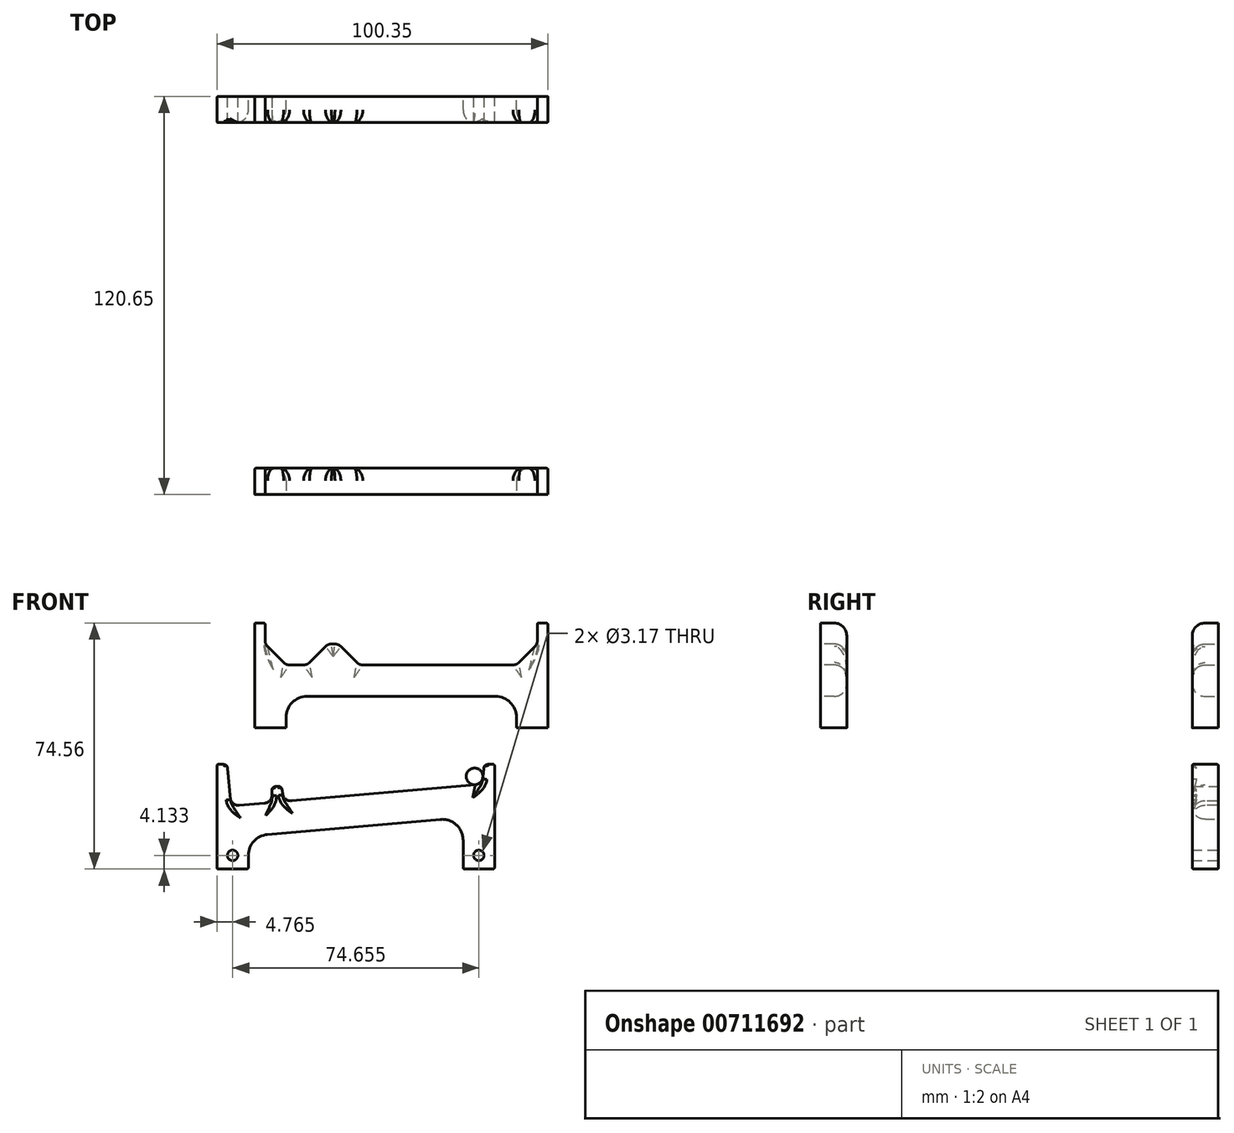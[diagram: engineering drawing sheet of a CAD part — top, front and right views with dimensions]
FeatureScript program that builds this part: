
annotation { "Feature Type Name" : "Feature", "Feature Type Description" : "" }
export const myFeature = defineFeature(function(context is Context, id is Id, definition is map)
    precondition{}
    {
        {
            var Q0;
            Q0=qCreatedBy(makeId("Front.planeOp"),FACE);
            var sketch = newSketch(context, id + "F0", { "sketchPlane" : qUnion([Q0])});
            skLineSegment(sketch, "E0", {"start": v(-44.45, 0) * mm, "end": v(-44.45, 25.4) * mm});
            skLineSegment(sketch, "E1", {"start": v(-28.58, 19.05) * mm, "end": v(-22.23, 25.4) * mm});
            skLineSegment(sketch, "E2", {"start": v(-22.23, 25.4) * mm, "end": v(-19.05, 25.4) * mm});
            skLineSegment(sketch, "E3", {"start": v(-19.05, 25.4) * mm, "end": v(-12.7, 19.05) * mm});
            skLineSegment(sketch, "E4", {"start": v(-12.7, 19.05) * mm, "end": v(34.92, 19.05) * mm});
            skLineSegment(sketch, "E5", {"start": v(34.92, 19.05) * mm, "end": v(41.28, 25.4) * mm});
            skLineSegment(sketch, "E6", {"start": v(44.45, 25.4) * mm, "end": v(44.45, 0) * mm});
            skLineSegment(sketch, "E7", {"start": v(-41.28, 25.4) * mm, "end": v(-34.93, 19.05) * mm});
            skLineSegment(sketch, "E8", {"start": v(-34.93, 19.05) * mm, "end": v(-28.58, 19.05) * mm});
            skLineSegment(sketch, "E9", {"start": v(-44.45, 25.4) * mm, "end": v(-44.45, 31.75) * mm});
            skLineSegment(sketch, "E10", {"start": v(-44.45, 31.75) * mm, "end": v(-41.28, 31.75) * mm});
            skLineSegment(sketch, "E11", {"start": v(-41.28, 31.75) * mm, "end": v(-41.28, 25.4) * mm});
            skLineSegment(sketch, "E12", {"start": v(44.45, 25.4) * mm, "end": v(44.45, 31.75) * mm});
            skLineSegment(sketch, "E13", {"start": v(44.45, 31.75) * mm, "end": v(41.28, 31.75) * mm});
            skLineSegment(sketch, "E14", {"start": v(41.28, 31.75) * mm, "end": v(41.28, 25.4) * mm});
            skLineSegment(sketch, "E15", {"start": v(-44.45, 0) * mm, "end": v(-34.93, 0) * mm});
            skLineSegment(sketch, "E16", {"start": v(44.45, 0) * mm, "end": v(34.92, 0) * mm});
            skLineSegment(sketch, "E17", {"start": v(-34.93, 0) * mm, "end": v(-34.93, 3.17) * mm});
            skLineSegment(sketch, "E18", {"start": v(34.92, 3.18) * mm, "end": v(34.92, 0) * mm});
            skPoint(sketch, "E19.visualSharp", {"position": v(-34.93, 9.52) * mm});
            skArc(sketch, "E19.filletArc", {"start": v(-28.58, 9.52) * mm, "mid": v(-33.07, 7.67) * mm, "end": v(-34.93, 3.17) * mm});
            skPoint(sketch, "E20.visualSharp", {"position": v(34.93, 9.53) * mm});
            skArc(sketch, "E20.filletArc", {"start": v(34.92, 3.18) * mm, "mid": v(33.07, 7.67) * mm, "end": v(28.58, 9.53) * mm});
            skLineSegment(sketch, "E21", {"start": v(-28.58, 9.52) * mm, "end": v(0, 9.52) * mm});
            skLineSegment(sketch, "E22", {"start": v(0, 9.52) * mm, "end": v(28.58, 9.53) * mm});
            skSolve(sketch);
        }
        {
            var Q0;
            Q0=makeQuery(id+"F0.imprint","IMPRINT",FACE,{"disambiguationData":[TD([[makeQuery(id+"F0.imprint","IMPRINT",EDGE,{"derivedFrom":sQuery(id+"F0.wireOp",EDGE,"E0")}),-1.0]])]});
            extrude(context, id + "F1", {"entities" : qUnion([Q0]), "depth" : 7.94 * mm, "offsetDistance" : 25.4 * mm});
        }
        {
            var Q0;
            Q0=makeQuery(id+"F1.opExtrude","CAP_EDGE",EDGE,{"disambiguationData":[OSD([sQuery(id+"F0.wireOp",EDGE,"E7")])],"isStart":false});
            var Q1;
            Q1=makeQuery(id+"F1.opExtrude","CAP_EDGE",EDGE,{"disambiguationData":[OSD([sQuery(id+"F0.wireOp",EDGE,"E8")])],"isStart":false});
            var Q2;
            Q2=makeQuery(id+"F1.opExtrude","CAP_EDGE",EDGE,{"disambiguationData":[OSD([sQuery(id+"F0.wireOp",EDGE,"E1")])],"isStart":false});
            var Q3;
            Q3=makeQuery(id+"F1.opExtrude","CAP_EDGE",EDGE,{"disambiguationData":[OSD([sQuery(id+"F0.wireOp",EDGE,"E2")])],"isStart":false});
            var Q4;
            Q4=makeQuery(id+"F1.opExtrude","CAP_EDGE",EDGE,{"disambiguationData":[OSD([sQuery(id+"F0.wireOp",EDGE,"E3")])],"isStart":false});
            var Q5;
            Q5=makeQuery(id+"F1.opExtrude","CAP_EDGE",EDGE,{"disambiguationData":[OSD([sQuery(id+"F0.wireOp",EDGE,"E4")])],"isStart":false});
            var Q6;
            Q6=makeQuery(id+"F1.opExtrude","CAP_EDGE",EDGE,{"disambiguationData":[OSD([sQuery(id+"F0.wireOp",EDGE,"E5")])],"isStart":false});
            var Q7;
            Q7=makeQuery(id+"F1.opExtrude","CAP_EDGE",EDGE,{"disambiguationData":[OSD([sQuery(id+"F0.wireOp",EDGE,"E10")])],"isStart":false});
            var Q8;
            Q8=makeQuery(id+"F1.opExtrude","CAP_EDGE",EDGE,{"disambiguationData":[OSD([sQuery(id+"F0.wireOp",EDGE,"E13")])],"isStart":false});
            var Q9;
            Q9=makeQuery(id+"F1.opExtrude","CAP_EDGE",EDGE,{"disambiguationData":[OSD([sQuery(id+"F0.wireOp",EDGE,"E21"),sQuery(id+"F0.wireOp",EDGE,"E22")])],"isStart":false});
            fillet(context, id + "F2", {"entities" : qUnion([Q0, Q1, Q2, Q3, Q4, Q5, Q6, Q7, Q8, Q9]), "radius" : 3.8 * mm, "tangentPropagation" : true, "allowEdgeOverflow" : false});
        }
        {
            var Q0;
            Q0=makeQuery(id+"F1.opExtrude","SWEPT_EDGE",EDGE,{"disambiguationData":[OSD([sQuery(id+"F0.wireOp",EDGE,"E1"),sQuery(id+"F0.wireOp",EDGE,"E2")])]});
            var Q1;
            Q1=makeQuery(id+"F1.opExtrude","SWEPT_EDGE",EDGE,{"disambiguationData":[OSD([sQuery(id+"F0.wireOp",EDGE,"E2"),sQuery(id+"F0.wireOp",EDGE,"E3")])]});
            var Q2;
            Q2=makeQuery(id+"F1.opExtrude","SWEPT_EDGE",EDGE,{"disambiguationData":[OSD([sQuery(id+"F0.wireOp",EDGE,"E1"),sQuery(id+"F0.wireOp",EDGE,"E8")])]});
            var Q3;
            Q3=makeQuery(id+"F1.opExtrude","SWEPT_EDGE",EDGE,{"disambiguationData":[OSD([sQuery(id+"F0.wireOp",EDGE,"E7"),sQuery(id+"F0.wireOp",EDGE,"E8")])]});
            var Q4;
            Q4=makeQuery(id+"F1.opExtrude","SWEPT_EDGE",EDGE,{"disambiguationData":[OSD([sQuery(id+"F0.wireOp",EDGE,"E3"),sQuery(id+"F0.wireOp",EDGE,"E4")])]});
            var Q5;
            Q5=makeQuery(id+"F1.opExtrude","SWEPT_EDGE",EDGE,{"disambiguationData":[OSD([sQuery(id+"F0.wireOp",EDGE,"E4"),sQuery(id+"F0.wireOp",EDGE,"E5")])]});
            var Q6;
            Q6=makeQuery(id+"F1.opExtrude","SWEPT_EDGE",EDGE,{"disambiguationData":[OSD([sQuery(id+"F0.wireOp",EDGE,"E5"),sQuery(id+"F0.wireOp",EDGE,"E14")])]});
            var Q7;
            Q7=makeQuery(id+"F1.opExtrude","SWEPT_EDGE",EDGE,{"disambiguationData":[OSD([sQuery(id+"F0.wireOp",EDGE,"E7"),sQuery(id+"F0.wireOp",EDGE,"E11")])]});
            fillet(context, id + "F3", {"entities" : qUnion([Q0, Q1, Q2, Q3, Q4, Q5, Q6, Q7]), "radius" : 2.54 * mm, "tangentPropagation" : true, "allowEdgeOverflow" : false});
        }
        {
            var Q0;
            Q0=makeQuery(id+"F1.opExtrude","CAP_EDGE",EDGE,{"disambiguationData":[OSD([sQuery(id+"F0.wireOp",EDGE,"E0"),sQuery(id+"F0.wireOp",EDGE,"E9")])],"isStart":false});
            var Q1;
            Q1=makeQuery(id+"F1.opExtrude","CAP_EDGE",EDGE,{"disambiguationData":[OSD([sQuery(id+"F0.wireOp",EDGE,"E6"),sQuery(id+"F0.wireOp",EDGE,"E12")])],"isStart":false});
            var Q2;
            Q2=makeQuery(id+"F2.opFillet","BLEND_EDGE",EDGE,{"blendedFrom":[makeQuery(id+"F1.opExtrude","CAP_EDGE",EDGE,{"disambiguationData":[OSD([sQuery(id+"F0.wireOp",EDGE,"E13")])],"isStart":false}),makeQuery(id+"F1.opExtrude","SWEPT_FACE",FACE,{"disambiguationData":[OSD([sQuery(id+"F0.wireOp",EDGE,"E14")])]})],"blendedInto":[makeQuery(id+"F1.opExtrude","SWEPT_FACE",FACE,{"disambiguationData":[OSD([sQuery(id+"F0.wireOp",EDGE,"E14")])]})]});
            var Q3;
            Q3=makeQuery(id+"F2.opFillet","BLEND_EDGE",EDGE,{"blendedFrom":[makeQuery(id+"F1.opExtrude","CAP_EDGE",EDGE,{"disambiguationData":[OSD([sQuery(id+"F0.wireOp",EDGE,"E10")])],"isStart":false}),makeQuery(id+"F1.opExtrude","SWEPT_FACE",FACE,{"disambiguationData":[OSD([sQuery(id+"F0.wireOp",EDGE,"E11")])]})],"blendedInto":[makeQuery(id+"F1.opExtrude","SWEPT_FACE",FACE,{"disambiguationData":[OSD([sQuery(id+"F0.wireOp",EDGE,"E11")])]})]});
            fillet(context, id + "F4", {"entities" : qUnion([Q0, Q1, Q2, Q3]), "radius" : 0.38 * mm, "tangentPropagation" : true, "allowEdgeOverflow" : false});
        }
        {
            var Q0;
            Q0=makeQuery(id+"F1.opExtrude","SWEPT_BODY",BODY,{"disambiguationData":[OSD([sQuery(id+"F0.wireOp",EDGE,"E0"),sQuery(id+"F0.wireOp",EDGE,"E1"),sQuery(id+"F0.wireOp",EDGE,"E2"),sQuery(id+"F0.wireOp",EDGE,"E3"),sQuery(id+"F0.wireOp",EDGE,"E4"),sQuery(id+"F0.wireOp",EDGE,"E5"),sQuery(id+"F0.wireOp",EDGE,"E6"),sQuery(id+"F0.wireOp",EDGE,"E7"),sQuery(id+"F0.wireOp",EDGE,"E8"),sQuery(id+"F0.wireOp",EDGE,"E9"),sQuery(id+"F0.wireOp",EDGE,"E10"),sQuery(id+"F0.wireOp",EDGE,"E11"),sQuery(id+"F0.wireOp",EDGE,"E12"),sQuery(id+"F0.wireOp",EDGE,"E13"),sQuery(id+"F0.wireOp",EDGE,"E14"),sQuery(id+"F0.wireOp",EDGE,"E15"),sQuery(id+"F0.wireOp",EDGE,"E16"),sQuery(id+"F0.wireOp",EDGE,"E17"),sQuery(id+"F0.wireOp",EDGE,"E18"),sQuery(id+"F0.wireOp",EDGE,"E19.filletArc"),sQuery(id+"F0.wireOp",EDGE,"E20.filletArc"),sQuery(id+"F0.wireOp",EDGE,"E21"),sQuery(id+"F0.wireOp",EDGE,"E22")])]});
            var Q1;
            Q1=qCreatedBy(makeId("Front.planeOp"),FACE);
            mirror(context, id + "F5", {"entities" : qUnion([Q0]), "mirrorPlane" : qUnion([Q1])});
        }
        {
            var Q0;
            Q0=makeQuery(id+"F5.opPattern","COPY",BODY,{"derivedFrom":makeQuery(id+"F1.opExtrude","SWEPT_BODY",BODY,{"disambiguationData":[OSD([sQuery(id+"F0.wireOp",EDGE,"E0"),sQuery(id+"F0.wireOp",EDGE,"E1"),sQuery(id+"F0.wireOp",EDGE,"E2"),sQuery(id+"F0.wireOp",EDGE,"E3"),sQuery(id+"F0.wireOp",EDGE,"E4"),sQuery(id+"F0.wireOp",EDGE,"E5"),sQuery(id+"F0.wireOp",EDGE,"E6"),sQuery(id+"F0.wireOp",EDGE,"E7"),sQuery(id+"F0.wireOp",EDGE,"E8"),sQuery(id+"F0.wireOp",EDGE,"E9"),sQuery(id+"F0.wireOp",EDGE,"E10"),sQuery(id+"F0.wireOp",EDGE,"E11"),sQuery(id+"F0.wireOp",EDGE,"E12"),sQuery(id+"F0.wireOp",EDGE,"E13"),sQuery(id+"F0.wireOp",EDGE,"E14"),sQuery(id+"F0.wireOp",EDGE,"E15"),sQuery(id+"F0.wireOp",EDGE,"E16"),sQuery(id+"F0.wireOp",EDGE,"E17"),sQuery(id+"F0.wireOp",EDGE,"E18"),sQuery(id+"F0.wireOp",EDGE,"E19.filletArc"),sQuery(id+"F0.wireOp",EDGE,"E20.filletArc"),sQuery(id+"F0.wireOp",EDGE,"E21"),sQuery(id+"F0.wireOp",EDGE,"E22")])]}),"instanceName":"1"});
            var Q1;
            Q1=qCreatedBy(makeId("Front.planeOp"),FACE);
            transform(context, id + "F6", {"entities" : qUnion([Q0]), "transformType" : TransformType.TRANSLATION_DISTANCE, "transformDirection" : qUnion([Q1]), "distance" : 120.65 * mm, "makeCopy" : false});
        }
        {
            var Q0;
            Q0=qCreatedBy(makeId("Front.planeOp"),FACE);
            var sketch = newSketch(context, id + "F7", { "sketchPlane" : qUnion([Q0])});
            skLineSegment(sketch, "E23", {"start": v(-39.38, -17.9) * mm, "end": v(-36.22, -17.63) * mm});
            skLineSegment(sketch, "E24", {"start": v(-39.38, -17.9) * mm, "end": v(-38.96, -22.65) * mm});
            skLineSegment(sketch, "E25", {"start": v(-38.96, -22.65) * mm, "end": v(-51.62, -23.76) * mm});
            skLineSegment(sketch, "E26", {"start": v(-51.62, -23.76) * mm, "end": v(-52.72, -11.1) * mm});
            skLineSegment(sketch, "E27", {"start": v(-52.72, -11.1) * mm, "end": v(-55.9, -11.1) * mm});
            skLineSegment(sketch, "E28", {"start": v(-55.9, -11.1) * mm, "end": v(-55.9, -42.8) * mm});
            skLineSegment(sketch, "E29", {"start": v(-36.22, -17.63) * mm, "end": v(-35.8, -22.37) * mm});
            skLineSegment(sketch, "E30", {"start": v(-55.9, -42.8) * mm, "end": v(-46.37, -42.8) * mm});
            skLineSegment(sketch, "E31", {"start": v(-46.37, -42.8) * mm, "end": v(-46.37, -38.68) * mm});
            skLineSegment(sketch, "E32", {"start": v(28.28, -42.8) * mm, "end": v(18.76, -42.8) * mm});
            skLineSegment(sketch, "E33", {"start": v(18.76, -42.8) * mm, "end": v(18.76, -38.68) * mm});
            skLineSegment(sketch, "E34", {"start": v(18.76, -38.68) * mm, "end": v(18.76, -34.09) * mm});
            skLineSegment(sketch, "E35", {"start": v(11.85, -27.76) * mm, "end": v(-40.58, -32.35) * mm});
            skLineSegment(sketch, "E36", {"start": v(28.28, -42.8) * mm, "end": v(28.28, -11.1) * mm});
            skLineSegment(sketch, "E37", {"start": v(28.28, -11.1) * mm, "end": v(25.1, -11.1) * mm});
            skLineSegment(sketch, "E38", {"start": v(-35.8, -22.37) * mm, "end": v(24.58, -17.09) * mm});
            skLineSegment(sketch, "E39", {"start": v(25.1, -11.1) * mm, "end": v(24.58, -17.09) * mm});
            skPoint(sketch, "E40.visualSharp", {"position": v(-46.37, -32.86) * mm});
            skArc(sketch, "E40.filletArc", {"start": v(-40.58, -32.35) * mm, "mid": v(-44.7, -34.39) * mm, "end": v(-46.37, -38.68) * mm});
            skPoint(sketch, "E41.visualSharp", {"position": v(18.76, -27.16) * mm});
            skArc(sketch, "E41.filletArc", {"start": v(18.76, -34.09) * mm, "mid": v(16.7, -29.4) * mm, "end": v(11.85, -27.76) * mm});
            skCircle(sketch, "E42", {"center": v(-51.14, -38.68) * mm, "radius": 1.59 * mm});
            skPoint(sketch, "E43", {"position": v(-51.14, -42.8) * mm});
            skCircle(sketch, "E44", {"center": v(23.52, -38.68) * mm, "radius": 1.59 * mm});
            skPoint(sketch, "E45", {"position": v(23.52, -42.8) * mm});
            skSolve(sketch);
        }
        {
            var Q0;
            Q0=makeQuery(id+"F7.imprint","IMPRINT",FACE,{"disambiguationData":[TD([[makeQuery(id+"F7.imprint","IMPRINT",EDGE,{"derivedFrom":sQuery(id+"F7.wireOp",EDGE,"E23")}),-1.0]])]});
            extrude(context, id + "F8", {"entities" : qUnion([Q0]), "depth" : 7.94 * mm, "offsetDistance" : 25.4 * mm});
        }
        {
            var Q0;
            Q0=makeQuery(id+"F8.opExtrude","CAP_EDGE",EDGE,{"disambiguationData":[OSD([sQuery(id+"F7.wireOp",EDGE,"E25")])],"isStart":false});
            var Q1;
            Q1=makeQuery(id+"F8.opExtrude","CAP_EDGE",EDGE,{"disambiguationData":[OSD([sQuery(id+"F7.wireOp",EDGE,"E38")])],"isStart":false});
            var Q2;
            Q2=makeQuery(id+"F8.opExtrude","CAP_EDGE",EDGE,{"disambiguationData":[OSD([sQuery(id+"F7.wireOp",EDGE,"E35")])],"isStart":false});
            fillet(context, id + "F9", {"entities" : qUnion([Q0, Q1, Q2]), "radius" : 3.8 * mm, "tangentPropagation" : true, "allowEdgeOverflow" : false});
        }
        {
            var Q0;
            Q0=makeQuery(id+"F8.opExtrude","SWEPT_EDGE",EDGE,{"disambiguationData":[OSD([sQuery(id+"F7.wireOp",EDGE,"E25"),sQuery(id+"F7.wireOp",EDGE,"E26")])]});
            var Q1;
            Q1=makeQuery(id+"F8.opExtrude","SWEPT_EDGE",EDGE,{"disambiguationData":[OSD([sQuery(id+"F7.wireOp",EDGE,"E24"),sQuery(id+"F7.wireOp",EDGE,"E25")])]});
            var Q2;
            Q2=makeQuery(id+"F8.opExtrude","SWEPT_EDGE",EDGE,{"disambiguationData":[OSD([sQuery(id+"F7.wireOp",EDGE,"E29"),sQuery(id+"F7.wireOp",EDGE,"E38")])]});
            var Q3;
            Q3=makeQuery(id+"F8.opExtrude","SWEPT_EDGE",EDGE,{"disambiguationData":[OSD([sQuery(id+"F7.wireOp",EDGE,"E38"),sQuery(id+"F7.wireOp",EDGE,"E39")])]});
            fillet(context, id + "F10", {"entities" : qUnion([Q0, Q1, Q2, Q3]), "radius" : 2.54 * mm, "tangentPropagation" : true, "allowEdgeOverflow" : false});
        }
        {
            var Q0;
            Q0=makeQuery(id+"F8.opExtrude","CAP_EDGE",EDGE,{"disambiguationData":[OSD([sQuery(id+"F7.wireOp",EDGE,"E26")])],"isStart":false});
            var Q1;
            Q1=makeQuery(id+"F8.opExtrude","SWEPT_EDGE",EDGE,{"disambiguationData":[OSD([sQuery(id+"F7.wireOp",EDGE,"E26"),sQuery(id+"F7.wireOp",EDGE,"E27")])]});
            var Q2;
            Q2=makeQuery(id+"F8.opExtrude","SWEPT_EDGE",EDGE,{"disambiguationData":[OSD([sQuery(id+"F7.wireOp",EDGE,"E23"),sQuery(id+"F7.wireOp",EDGE,"E24")])]});
            var Q3;
            Q3=makeQuery(id+"F8.opExtrude","SWEPT_EDGE",EDGE,{"disambiguationData":[OSD([sQuery(id+"F7.wireOp",EDGE,"E23"),sQuery(id+"F7.wireOp",EDGE,"E29")])]});
            var Q4;
            Q4=makeQuery(id+"F8.opExtrude","SWEPT_EDGE",EDGE,{"disambiguationData":[OSD([sQuery(id+"F7.wireOp",EDGE,"E37"),sQuery(id+"F7.wireOp",EDGE,"E39")])]});
            var Q5;
            Q5=makeQuery(id+"F8.opExtrude","CAP_EDGE",EDGE,{"disambiguationData":[OSD([sQuery(id+"F7.wireOp",EDGE,"E39")])],"isStart":false});
            var Q6;
            Q6=makeQuery(id+"F8.opExtrude","CAP_EDGE",EDGE,{"disambiguationData":[OSD([sQuery(id+"F7.wireOp",EDGE,"E24")])],"isStart":false});
            var Q7;
            Q7=makeQuery(id+"F8.opExtrude","CAP_EDGE",EDGE,{"disambiguationData":[OSD([sQuery(id+"F7.wireOp",EDGE,"E29")])],"isStart":false});
            fillet(context, id + "F11", {"entities" : qUnion([Q0, Q1, Q2, Q3, Q4, Q5, Q6, Q7]), "radius" : 1.27 * mm, "tangentPropagation" : true, "allowEdgeOverflow" : false});
        }
        {
            var Q0;
            Q0=makeQuery(id+"F8.opExtrude","CAP_EDGE",EDGE,{"disambiguationData":[OSD([sQuery(id+"F7.wireOp",EDGE,"E27")])],"isStart":false});
            var Q1;
            Q1=makeQuery(id+"F8.opExtrude","SWEPT_EDGE",EDGE,{"disambiguationData":[OSD([sQuery(id+"F7.wireOp",EDGE,"E27"),sQuery(id+"F7.wireOp",EDGE,"E28")])]});
            var Q2;
            Q2=makeQuery(id+"F8.opExtrude","CAP_EDGE",EDGE,{"disambiguationData":[OSD([sQuery(id+"F7.wireOp",EDGE,"E28")])],"isStart":false});
            var Q3;
            Q3=makeQuery(id+"F8.opExtrude","CAP_EDGE",EDGE,{"disambiguationData":[OSD([sQuery(id+"F7.wireOp",EDGE,"E36")])],"isStart":false});
            var Q4;
            Q4=makeQuery(id+"F8.opExtrude","SWEPT_EDGE",EDGE,{"disambiguationData":[OSD([sQuery(id+"F7.wireOp",EDGE,"E36"),sQuery(id+"F7.wireOp",EDGE,"E37")])]});
            var Q5;
            Q5=makeQuery(id+"F8.opExtrude","CAP_EDGE",EDGE,{"disambiguationData":[OSD([sQuery(id+"F7.wireOp",EDGE,"E23")])],"isStart":false});
            var Q6;
            Q6=makeQuery(id+"F8.opExtrude","CAP_EDGE",EDGE,{"disambiguationData":[OSD([sQuery(id+"F7.wireOp",EDGE,"E37")])],"isStart":false});
            var Q7;
            Q7=makeQuery(id+"F8.opExtrude","CAP_EDGE",EDGE,{"disambiguationData":[OSD([sQuery(id+"F7.wireOp",EDGE,"E36")])],"isStart":true});
            var Q8;
            Q8=makeQuery(id+"F8.opExtrude","SWEPT_EDGE",EDGE,{"disambiguationData":[OSD([sQuery(id+"F7.wireOp",EDGE,"E32"),sQuery(id+"F7.wireOp",EDGE,"E36")])]});
            var Q9;
            Q9=makeQuery(id+"F8.opExtrude","CAP_EDGE",EDGE,{"disambiguationData":[OSD([sQuery(id+"F7.wireOp",EDGE,"E32")])],"isStart":true});
            var Q10;
            Q10=makeQuery(id+"F8.opExtrude","CAP_EDGE",EDGE,{"disambiguationData":[OSD([sQuery(id+"F7.wireOp",EDGE,"E35")])],"isStart":true});
            var Q11;
            Q11=makeQuery(id+"F8.opExtrude","CAP_EDGE",EDGE,{"disambiguationData":[OSD([sQuery(id+"F7.wireOp",EDGE,"E38")])],"isStart":true});
            var Q12;
            Q12=makeQuery(id+"F8.opExtrude","CAP_EDGE",EDGE,{"disambiguationData":[OSD([sQuery(id+"F7.wireOp",EDGE,"E28")])],"isStart":true});
            var Q13;
            Q13=makeQuery(id+"F8.opExtrude","CAP_EDGE",EDGE,{"disambiguationData":[OSD([sQuery(id+"F7.wireOp",EDGE,"E30")])],"isStart":true});
            var Q14;
            Q14=makeQuery(id+"F8.opExtrude","SWEPT_EDGE",EDGE,{"disambiguationData":[OSD([sQuery(id+"F7.wireOp",EDGE,"E28"),sQuery(id+"F7.wireOp",EDGE,"E30")])]});
            var Q15;
            Q15=makeQuery(id+"F8.opExtrude","CAP_EDGE",EDGE,{"disambiguationData":[OSD([sQuery(id+"F7.wireOp",EDGE,"E32")])],"isStart":false});
            var Q16;
            Q16=makeQuery(id+"F8.opExtrude","CAP_EDGE",EDGE,{"disambiguationData":[OSD([sQuery(id+"F7.wireOp",EDGE,"E30")])],"isStart":false});
            fillet(context, id + "F12", {"entities" : qUnion([Q0, Q1, Q2, Q3, Q4, Q5, Q6, Q7, Q8, Q9, Q10, Q11, Q12, Q13, Q14, Q15, Q16]), "radius" : 0.38 * mm, "tangentPropagation" : true, "allowEdgeOverflow" : false});
        }
    });
